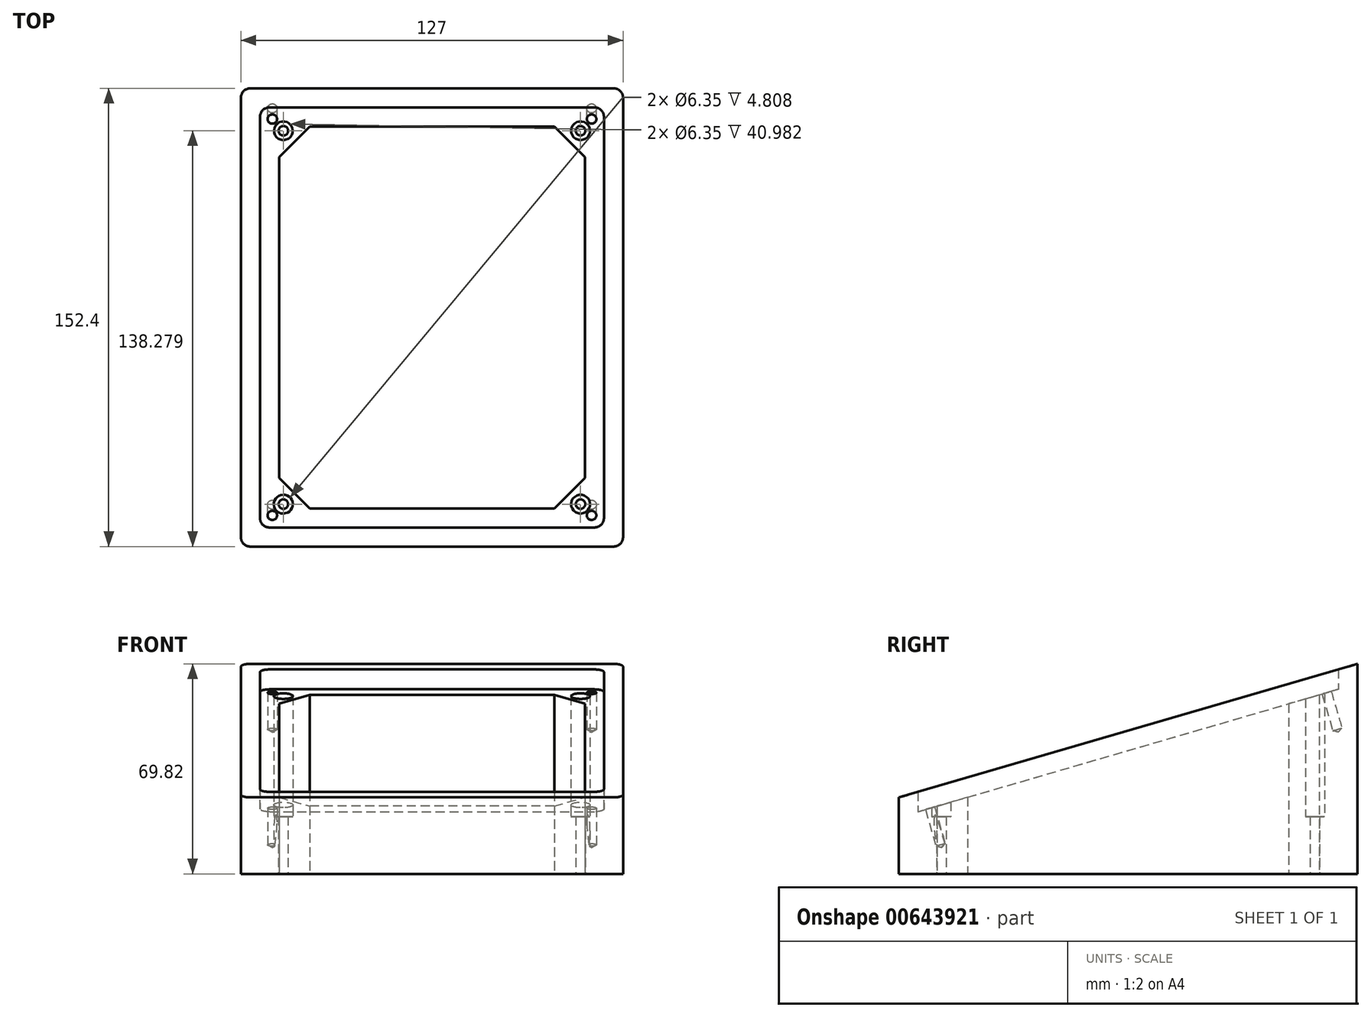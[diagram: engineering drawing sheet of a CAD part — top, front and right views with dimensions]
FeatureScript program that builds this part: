
annotation { "Feature Type Name" : "Feature", "Feature Type Description" : "" }
export const myFeature = defineFeature(function(context is Context, id is Id, definition is map)
    precondition{}
    {
        {
            var Q0;
            Q0=qCreatedBy(makeId("Top.planeOp"),FACE);
            var sketch = newSketch(context, id + "F0", { "sketchPlane" : qUnion([Q0])});
            skLineSegment(sketch, "E0.bottom", {"start": v(-63.5, 77.08) * mm, "end": v(63.5, 77.08) * mm});
            skLineSegment(sketch, "E0.top", {"start": v(-63.5, -75.32) * mm, "end": v(63.5, -75.32) * mm});
            skLineSegment(sketch, "E0.left", {"start": v(-63.5, 77.08) * mm, "end": v(-63.5, -75.32) * mm});
            skLineSegment(sketch, "E0.right", {"start": v(63.5, 77.08) * mm, "end": v(63.5, -75.32) * mm});
            skPoint(sketch, "E0.middle", {"position": v(0, 0.88) * mm});
            skLineSegment(sketch, "E1.bottom", {"start": v(-53.98, 70.73) * mm, "end": v(53.97, 70.73) * mm});
            skLineSegment(sketch, "E1.top", {"start": v(-53.98, -68.97) * mm, "end": v(53.97, -68.97) * mm});
            skLineSegment(sketch, "E1.left", {"start": v(-57.15, 67.56) * mm, "end": v(-57.15, -65.8) * mm});
            skLineSegment(sketch, "E1.right", {"start": v(57.15, 67.56) * mm, "end": v(57.15, -65.8) * mm});
            skLineSegment(sketch, "E2.bottom", {"start": v(-47.63, 64.38) * mm, "end": v(47.62, 64.38) * mm});
            skLineSegment(sketch, "E2.top", {"start": v(-47.63, -62.62) * mm, "end": v(48.25, -62.62) * mm});
            skLineSegment(sketch, "E2.left", {"start": v(-50.8, 61.2) * mm, "end": v(-50.8, -59.44) * mm});
            skLineSegment(sketch, "E2.right", {"start": v(50.8, 61.2) * mm, "end": v(50.8, -60.07) * mm});
            skPoint(sketch, "E3.visualSharp", {"position": v(-57.15, 70.73) * mm});
            skArc(sketch, "E3.filletArc", {"start": v(-53.98, 70.73) * mm, "mid": v(-56.22, 69.8) * mm, "end": v(-57.15, 67.56) * mm});
            skPoint(sketch, "E4.visualSharp", {"position": v(57.15, 70.73) * mm});
            skArc(sketch, "E4.filletArc", {"start": v(57.15, 67.56) * mm, "mid": v(56.22, 69.8) * mm, "end": v(53.97, 70.73) * mm});
            skPoint(sketch, "E5.visualSharp", {"position": v(57.15, -68.97) * mm});
            skArc(sketch, "E5.filletArc", {"start": v(53.97, -68.97) * mm, "mid": v(56.22, -68.04) * mm, "end": v(57.15, -65.8) * mm});
            skPoint(sketch, "E6.visualSharp", {"position": v(-57.15, -68.97) * mm});
            skArc(sketch, "E6.filletArc", {"start": v(-57.15, -65.8) * mm, "mid": v(-56.22, -68.04) * mm, "end": v(-53.98, -68.97) * mm});
            skPoint(sketch, "E7.visualSharp", {"position": v(50.8, 64.38) * mm});
            skArc(sketch, "E7.filletArc", {"start": v(50.8, 61.2) * mm, "mid": v(49.87, 63.45) * mm, "end": v(47.62, 64.38) * mm});
            skPoint(sketch, "E8.visualSharp", {"position": v(50.8, -62.62) * mm});
            skArc(sketch, "E8.filletArc", {"start": v(48.25, -62.62) * mm, "mid": v(50.05, -61.87) * mm, "end": v(50.8, -60.07) * mm});
            skPoint(sketch, "E9.visualSharp", {"position": v(-50.8, -62.62) * mm});
            skArc(sketch, "E9.filletArc", {"start": v(-50.8, -59.44) * mm, "mid": v(-49.87, -61.69) * mm, "end": v(-47.63, -62.62) * mm});
            skArc(sketch, "E10.filletArc", {"start": v(-47.63, 64.38) * mm, "mid": v(-49.87, 63.45) * mm, "end": v(-50.8, 61.2) * mm});
            skPoint(sketch, "E11.visualSharp", {"position": v(-63.5, 77.08) * mm});
            skLineSegment(sketch, "E11.filletArc", {"start": v(-63.5, 77.08) * mm, "end": v(-63.5, 77.08) * mm});
            skPoint(sketch, "E12.visualSharp", {"position": v(63.5, 77.08) * mm});
            skLineSegment(sketch, "E12.filletArc", {"start": v(63.5, 77.08) * mm, "end": v(63.5, 77.08) * mm});
            skPoint(sketch, "E13.visualSharp", {"position": v(63.5, -75.32) * mm});
            skLineSegment(sketch, "E13.filletArc", {"start": v(63.5, -75.32) * mm, "end": v(63.5, -75.32) * mm});
            skPoint(sketch, "E14.visualSharp", {"position": v(-63.5, -75.32) * mm});
            skLineSegment(sketch, "E14.filletArc", {"start": v(-63.5, -75.32) * mm, "end": v(-63.5, -75.32) * mm});
            skPoint(sketch, "E15", {"position": v(15.87, 64.38) * mm});
            skPoint(sketch, "E16", {"position": v(15.87, 77.08) * mm});
            skPoint(sketch, "E17", {"position": v(15.87, -62.62) * mm});
            skPoint(sketch, "E18", {"position": v(15.87, -75.32) * mm});
            skPoint(sketch, "E19", {"position": v(-15.88, 77.08) * mm});
            skPoint(sketch, "E20", {"position": v(-15.88, 64.38) * mm});
            skPoint(sketch, "E21", {"position": v(-15.88, -62.62) * mm});
            skPoint(sketch, "E22", {"position": v(-15.88, -75.32) * mm});
            skPoint(sketch, "E23", {"position": v(0, 77.08) * mm});
            skPoint(sketch, "E24", {"position": v(0, -75.32) * mm});
            skPoint(sketch, "E25", {"position": v(-63.5, 0.88) * mm});
            skPoint(sketch, "E26", {"position": v(63.5, 0.88) * mm});
            skPoint(sketch, "E27", {"position": v(63.5, 16.76) * mm});
            skPoint(sketch, "E28", {"position": v(50.8, 16.76) * mm});
            skPoint(sketch, "E29", {"position": v(-50.8, 16.76) * mm});
            skPoint(sketch, "E30", {"position": v(-63.5, 16.76) * mm});
            skPoint(sketch, "E31", {"position": v(63.5, -15) * mm});
            skPoint(sketch, "E32", {"position": v(50.8, -15) * mm});
            skPoint(sketch, "E33", {"position": v(-50.8, -15) * mm});
            skPoint(sketch, "E34", {"position": v(-63.5, -15) * mm});
            skPoint(sketch, "E35", {"position": v(40.64, 64.38) * mm});
            skPoint(sketch, "E36", {"position": v(40.64, -62.62) * mm});
            skPoint(sketch, "E37", {"position": v(-40.64, 64.38) * mm});
            skPoint(sketch, "E38", {"position": v(-40.64, -62.62) * mm});
            skPoint(sketch, "E39", {"position": v(-50.8, -52.46) * mm});
            skPoint(sketch, "E40", {"position": v(50.8, -52.46) * mm});
            skPoint(sketch, "E41", {"position": v(50.8, 54.22) * mm});
            skPoint(sketch, "E42", {"position": v(-50.8, 54.22) * mm});
            skLineSegment(sketch, "E43", {"start": v(-50.8, 54.22) * mm, "end": v(-40.64, 64.38) * mm});
            skLineSegment(sketch, "E44", {"start": v(40.64, 64.38) * mm, "end": v(50.8, 54.22) * mm});
            skLineSegment(sketch, "E45", {"start": v(50.8, -52.46) * mm, "end": v(40.64, -62.62) * mm});
            skLineSegment(sketch, "E46", {"start": v(-40.64, -62.62) * mm, "end": v(-50.8, -52.46) * mm});
            skPoint(sketch, "E47", {"position": v(-45.72, 59.3) * mm});
            skPoint(sketch, "E48", {"position": v(45.72, 59.3) * mm});
            skPoint(sketch, "E49", {"position": v(45.72, -57.54) * mm});
            skPoint(sketch, "E50", {"position": v(-45.72, -57.54) * mm});
            skPoint(sketch, "E51", {"position": v(30.16, 77.08) * mm});
            skPoint(sketch, "E52", {"position": v(30.16, 64.38) * mm});
            skPoint(sketch, "E53", {"position": v(30.16, -62.62) * mm});
            skPoint(sketch, "E54", {"position": v(30.16, -75.32) * mm});
            skPoint(sketch, "E55", {"position": v(-30.16, 77.08) * mm});
            skPoint(sketch, "E56", {"position": v(-30.16, 64.38) * mm});
            skPoint(sketch, "E57", {"position": v(-30.16, -62.62) * mm});
            skPoint(sketch, "E58", {"position": v(-30.16, -75.32) * mm});
            skPoint(sketch, "E59", {"position": v(63.5, 37.4) * mm});
            skPoint(sketch, "E60", {"position": v(50.8, 37.4) * mm});
            skPoint(sketch, "E61", {"position": v(-50.8, 37.4) * mm});
            skPoint(sketch, "E62", {"position": v(-63.5, 37.4) * mm});
            skPoint(sketch, "E63", {"position": v(63.5, -35.63) * mm});
            skPoint(sketch, "E64", {"position": v(50.8, -35.63) * mm});
            skPoint(sketch, "E65", {"position": v(-50.8, -35.63) * mm});
            skPoint(sketch, "E66", {"position": v(-63.5, -35.63) * mm});
            skPoint(sketch, "E67", {"position": v(-36.51, 77.08) * mm});
            skPoint(sketch, "E68", {"position": v(-36.51, 64.38) * mm});
            skPoint(sketch, "E69", {"position": v(-36.51, -62.62) * mm});
            skPoint(sketch, "E70", {"position": v(-36.51, -75.32) * mm});
            skPoint(sketch, "E71", {"position": v(36.51, 77.08) * mm});
            skPoint(sketch, "E72", {"position": v(36.51, 64.38) * mm});
            skPoint(sketch, "E73", {"position": v(36.51, -62.62) * mm});
            skPoint(sketch, "E74", {"position": v(36.51, -75.32) * mm});
            skPoint(sketch, "E75", {"position": v(-23.81, 77.08) * mm});
            skPoint(sketch, "E76", {"position": v(-23.81, 64.38) * mm});
            skPoint(sketch, "E77", {"position": v(23.81, 77.08) * mm});
            skPoint(sketch, "E78", {"position": v(23.81, 64.38) * mm});
            skPoint(sketch, "E79", {"position": v(23.81, -62.62) * mm});
            skPoint(sketch, "E80", {"position": v(23.81, -75.32) * mm});
            skPoint(sketch, "E81", {"position": v(-23.81, -62.62) * mm});
            skPoint(sketch, "E82", {"position": v(-23.81, -75.32) * mm});
            skPoint(sketch, "E83", {"position": v(-63.5, 43.74) * mm});
            skPoint(sketch, "E84", {"position": v(-50.8, 43.74) * mm});
            skPoint(sketch, "E85", {"position": v(50.8, 43.74) * mm});
            skPoint(sketch, "E86", {"position": v(63.5, 43.74) * mm});
            skPoint(sketch, "E87", {"position": v(-63.5, 31.04) * mm});
            skPoint(sketch, "E88", {"position": v(-50.8, 31.04) * mm});
            skPoint(sketch, "E89", {"position": v(50.8, 31.04) * mm});
            skPoint(sketch, "E90", {"position": v(63.5, 31.04) * mm});
            skPoint(sketch, "E91", {"position": v(-63.5, -29.28) * mm});
            skPoint(sketch, "E92", {"position": v(-50.8, -29.28) * mm});
            skPoint(sketch, "E93", {"position": v(50.8, -29.28) * mm});
            skPoint(sketch, "E94", {"position": v(63.5, -29.28) * mm});
            skPoint(sketch, "E95", {"position": v(-63.5, -41.98) * mm});
            skPoint(sketch, "E96", {"position": v(-50.8, -41.98) * mm});
            skPoint(sketch, "E97", {"position": v(50.8, -41.98) * mm});
            skPoint(sketch, "E98", {"position": v(63.5, -41.98) * mm});
            skLineSegment(sketch, "E99", {"start": v(57.15, 70.73) * mm, "end": v(45.72, 59.3) * mm, "construction": true});
            skLineSegment(sketch, "E100", {"start": v(57.15, -68.97) * mm, "end": v(45.72, -57.54) * mm, "construction": true});
            skLineSegment(sketch, "E101", {"start": v(-57.15, -68.97) * mm, "end": v(-45.72, -57.54) * mm, "construction": true});
            skPoint(sketch, "E102", {"position": v(53.04, 66.62) * mm});
            skLineSegment(sketch, "E103", {"start": v(-57.15, 70.73) * mm, "end": v(-45.72, 59.3) * mm, "construction": true});
            skPoint(sketch, "E104", {"position": v(-53.04, 66.62) * mm});
            skPoint(sketch, "E105", {"position": v(53.04, -64.86) * mm});
            skPoint(sketch, "E106", {"position": v(-53.04, -64.86) * mm});
            skCircle(sketch, "E107", {"center": v(-53.04, 66.62) * mm, "radius": 1.59 * mm});
            skCircle(sketch, "E108", {"center": v(53.04, 66.62) * mm, "radius": 1.59 * mm});
            skCircle(sketch, "E109", {"center": v(53.04, -64.86) * mm, "radius": 1.59 * mm});
            skCircle(sketch, "E110", {"center": v(-53.04, -64.86) * mm, "radius": 1.59 * mm});
            skPoint(sketch, "E111", {"position": v(-49.38, -61.2) * mm});
            skPoint(sketch, "E112", {"position": v(49.38, -61.2) * mm});
            skCircle(sketch, "E113", {"center": v(-49.38, -61.2) * mm, "radius": 1.59 * mm});
            skCircle(sketch, "E114", {"center": v(49.38, -61.2) * mm, "radius": 1.59 * mm});
            skPoint(sketch, "E115", {"position": v(-49.38, 62.96) * mm});
            skPoint(sketch, "E116", {"position": v(49.38, 62.96) * mm});
            skCircle(sketch, "E117", {"center": v(-49.38, 62.96) * mm, "radius": 1.59 * mm});
            skCircle(sketch, "E118", {"center": v(49.38, 62.96) * mm, "radius": 1.59 * mm});
            skCircle(sketch, "E119", {"center": v(-49.38, 62.96) * mm, "radius": 3.18 * mm});
            skCircle(sketch, "E120", {"center": v(49.38, 62.96) * mm, "radius": 3.18 * mm});
            skCircle(sketch, "E121", {"center": v(-49.38, -61.2) * mm, "radius": 3.18 * mm});
            skCircle(sketch, "E122", {"center": v(49.38, -61.2) * mm, "radius": 3.18 * mm});
            skSolve(sketch);
        }
        {
            var Q0;
            Q0=makeQuery(id+"F0.imprint","IMPRINT",FACE,{"disambiguationData":[TD([[makeQuery(id+"F0.imprint","IMPRINT",EDGE,{"derivedFrom":sQuery(id+"F0.wireOp",EDGE,"E0.bottom")}),-1.0]])]});
            var Q1;
            Q1=makeQuery(id+"F0.imprint","IMPRINT",FACE,{"disambiguationData":[TD([[makeQuery(id+"F0.imprint","IMPRINT",EDGE,{"derivedFrom":sQuery(id+"F0.wireOp",EDGE,"E1.bottom")}),-1.0]])]});
            var Q2;
            {var subQ5=sQuery(id+"F0.wireOp",EDGE,"E43");Q2=makeQuery(id+"F0.imprint","IMPRINT",FACE,{"disambiguationData":[TD([[makeQuery(id+"F0.imprint","IMPRINT",EDGE,{"derivedFrom":subQ5}),1.0]])]});}
            var Q3;
            {var subQ8=sQuery(id+"F0.wireOp",EDGE,"E44");Q3=makeQuery(id+"F0.imprint","IMPRINT",FACE,{"disambiguationData":[TD([[makeQuery(id+"F0.imprint","IMPRINT",EDGE,{"derivedFrom":subQ8}),1.0]])]});}
            var Q4;
            {var subQ8=sQuery(id+"F0.wireOp",EDGE,"E45");Q4=makeQuery(id+"F0.imprint","IMPRINT",FACE,{"disambiguationData":[TD([[makeQuery(id+"F0.imprint","IMPRINT",EDGE,{"derivedFrom":subQ8}),1.0]])]});}
            var Q5;
            {var subQ5=sQuery(id+"F0.wireOp",EDGE,"E46");Q5=makeQuery(id+"F0.imprint","IMPRINT",FACE,{"disambiguationData":[TD([[makeQuery(id+"F0.imprint","IMPRINT",EDGE,{"derivedFrom":subQ5}),1.0]])]});}
            var Q6;
            Q6=makeQuery(id+"F0.imprint","IMPRINT",FACE,{"disambiguationData":[TD([[makeQuery(id+"F0.imprint","IMPRINT",EDGE,{"derivedFrom":sQuery(id+"F0.wireOp",EDGE,"E108")}),1.0]])]});
            var Q7;
            Q7=makeQuery(id+"F0.imprint","IMPRINT",FACE,{"disambiguationData":[TD([[makeQuery(id+"F0.imprint","IMPRINT",EDGE,{"derivedFrom":sQuery(id+"F0.wireOp",EDGE,"E107")}),1.0]])]});
            var Q8;
            Q8=makeQuery(id+"F0.imprint","IMPRINT",FACE,{"disambiguationData":[TD([[makeQuery(id+"F0.imprint","IMPRINT",EDGE,{"derivedFrom":sQuery(id+"F0.wireOp",EDGE,"E109")}),1.0]])]});
            var Q9;
            Q9=makeQuery(id+"F0.imprint","IMPRINT",FACE,{"disambiguationData":[TD([[makeQuery(id+"F0.imprint","IMPRINT",EDGE,{"derivedFrom":sQuery(id+"F0.wireOp",EDGE,"E110")}),1.0]])]});
            extrude(context, id + "F1", {"entities" : qUnion([Q0, Q1, Q2, Q3, Q4, Q5, Q6, Q7, Q8, Q9]), "depth" : 76.2 * mm, "offsetDistance" : 25.4 * mm});
        }
        {
            var Q0;
            Q0=makeQuery(id+"F1.opExtrude","SWEPT_FACE",FACE,{"disambiguationData":[OSD([sQuery(id+"F0.wireOp",EDGE,"E0.right")])]});
            var sketch = newSketch(context, id + "F2", { "sketchPlane" : qUnion([Q0])});
            skPoint(sketch, "E123", {"position": v(77.08, 25.4) * mm});
            skPoint(sketch, "E124", {"position": v(77.08, 69.85) * mm});
            skPoint(sketch, "E125", {"position": v(-75.38, 25.4) * mm});
            skPoint(sketch, "E126", {"position": v(77.18, 69.85) * mm});
            skLineSegment(sketch, "E127", {"start": v(-75.38, 25.4) * mm, "end": v(77.18, 69.85) * mm});
            skLineSegment(sketch, "E128", {"start": v(77.18, 69.85) * mm, "end": v(77.18, 82.96) * mm});
            skLineSegment(sketch, "E129", {"start": v(77.18, 82.96) * mm, "end": v(-75.38, 82.96) * mm});
            skLineSegment(sketch, "E130", {"start": v(-75.38, 82.96) * mm, "end": v(-75.38, 25.4) * mm});
            skSolve(sketch);
        }
        {
            var Q0;
            Q0 = qSketchRegion(id + "F2", true);
            extrude(context, id + "F3", {"entities" : qUnion([Q0]), "operationType" : NewBodyOperationType.REMOVE, "oppositeDirection" : true, "depth" : 133.86 * mm, "offsetDistance" : 25.4 * mm});
        }
        {
            var Q0;
            Q0=makeQuery(id+"F1.opExtrude","SWEPT_FACE",FACE,{"disambiguationData":[OSD([sQuery(id+"F0.wireOp",EDGE,"E0.right")])]});
            var sketch = newSketch(context, id + "F4", { "sketchPlane" : qUnion([Q0])});
            skPoint(sketch, "E131", {"position": v(-75.32, 19.07) * mm});
            skPoint(sketch, "E132", {"position": v(-68.97, 19.07) * mm});
            skPoint(sketch, "E133", {"position": v(77.08, 63.47) * mm});
            skPoint(sketch, "E134", {"position": v(-68.97, 27.27) * mm});
            skPoint(sketch, "E135", {"position": v(70.73, 67.97) * mm});
            skPoint(sketch, "E136", {"position": v(-68.97, 20.66) * mm});
            skPoint(sketch, "E137", {"position": v(70.73, 61.36) * mm});
            skPoint(sketch, "E138", {"position": v(70.73, 71.15) * mm});
            skPoint(sketch, "E139", {"position": v(-68.97, 30.44) * mm});
            skLineSegment(sketch, "E140", {"start": v(-68.97, 20.66) * mm, "end": v(70.73, 61.36) * mm});
            skLineSegment(sketch, "E141", {"start": v(70.73, 71.15) * mm, "end": v(70.73, 61.36) * mm});
            skLineSegment(sketch, "E142", {"start": v(-68.97, 30.44) * mm, "end": v(-68.97, 20.66) * mm});
            skLineSegment(sketch, "E143", {"start": v(-68.97, 30.44) * mm, "end": v(70.73, 71.15) * mm});
            skPoint(sketch, "E144", {"position": v(-75.32, 25.42) * mm});
            skPoint(sketch, "E145", {"position": v(-75.32, 0) * mm});
            skPoint(sketch, "E146", {"position": v(77.08, 69.82) * mm});
            skPoint(sketch, "E147", {"position": v(77.08, 0) * mm});
            skSolve(sketch);
        }
        {
            var Q0;
            {var subQ0=sQuery(id+"F4.wireOp",EDGE,"E140");Q0=makeQuery(id+"F4.imprint","IMPRINT",FACE,{"disambiguationData":[TD([[makeQuery(id+"F4.imprint","IMPRINT",EDGE,{"derivedFrom":subQ0}),1.0]])]});}
            var Q1;
            {var subQ0=sQuery(id+"F4.wireOp",EDGE,"E143");Q1=makeQuery(id+"F4.imprint","IMPRINT",FACE,{"disambiguationData":[TD([[makeQuery(id+"F4.imprint","IMPRINT",EDGE,{"derivedFrom":subQ0}),-1.0]])]});}
            extrude(context, id + "F5", {"entities" : qUnion([Q0, Q1]), "operationType" : NewBodyOperationType.REMOVE, "oppositeDirection" : true, "depth" : 120.65 * mm, "offsetDistance" : 25.4 * mm, "hasSecondDirection" : true, "secondDirectionOppositeDirection" : true, "secondDirectionDepth" : 6.35 * mm});
        }
        {
            var Q0;
            Q0=makeQuery(id+"F5.boolean.opBoolean","COPY",FACE,{"derivedFrom":makeQuery(id+"F5.opExtrude","SWEPT_FACE",FACE,{"disambiguationData":[OSD([sQuery(id+"F4.wireOp",EDGE,"E140")])]})});
            var sketch = newSketch(context, id + "F6", { "sketchPlane" : qUnion([Q0])});
            skPoint(sketch, "E148", {"position": v(-57.15, 85.07) * mm});
            skPoint(sketch, "E149", {"position": v(57.15, 85.07) * mm});
            skPoint(sketch, "E150", {"position": v(57.15, -60.44) * mm});
            skPoint(sketch, "E151", {"position": v(-57.15, -60.44) * mm});
            skPoint(sketch, "E152", {"position": v(-53.04, 81.03) * mm});
            skPoint(sketch, "E153", {"position": v(53.04, 81.03) * mm});
            skPoint(sketch, "E154", {"position": v(53.04, -56.25) * mm});
            skPoint(sketch, "E155", {"position": v(-53.04, -56.25) * mm});
            skSolve(sketch);
        }
        {
            var Q0;
            Q0=sQuery(id+"F6.wireOp",VERTEX,"E152");
            var Q1;
            Q1=sQuery(id+"F6.wireOp",VERTEX,"E153");
            var Q2;
            Q2=sQuery(id+"F6.wireOp",VERTEX,"E154");
            var Q3;
            Q3=sQuery(id+"F6.wireOp",VERTEX,"E155");
            var Q4;
            Q4=makeQuery(id+"F1.opExtrude","SWEPT_BODY",BODY,{"disambiguationData":[OSD([sQuery(id+"F0.wireOp",EDGE,"E0.bottom"),sQuery(id+"F0.wireOp",EDGE,"E0.top"),sQuery(id+"F0.wireOp",EDGE,"E0.left"),sQuery(id+"F0.wireOp",EDGE,"E0.right"),sQuery(id+"F0.wireOp",EDGE,"E2.bottom"),sQuery(id+"F0.wireOp",EDGE,"E2.top"),sQuery(id+"F0.wireOp",EDGE,"E2.left"),sQuery(id+"F0.wireOp",EDGE,"E2.right"),sQuery(id+"F0.wireOp",EDGE,"E43"),sQuery(id+"F0.wireOp",EDGE,"E44"),sQuery(id+"F0.wireOp",EDGE,"E45"),sQuery(id+"F0.wireOp",EDGE,"E46"),sQuery(id+"F0.wireOp",EDGE,"E113"),sQuery(id+"F0.wireOp",EDGE,"E114"),sQuery(id+"F0.wireOp",EDGE,"E117"),sQuery(id+"F0.wireOp",EDGE,"E118")])]});
            hole(context, id + "F7", {"style" : HoleStyle.SIMPLE, "endStyle" : HoleEndStyle.BLIND, "holeDiameter" : 3.17 * mm, "majorDiameter" : 6.35 * mm, "holeDepth" : 12.7 * mm, "isTappedThrough" : true, "tappedDepth" : 12.7 * mm, "tapClearance" : 3, "locations" : qUnion([Q0, Q1, Q2, Q3]), "scope" : qUnion([Q4])});
        }
        {
            var Q0;
            Q0=makeQuery(id+"F5.boolean.opBoolean","COPY",EDGE,{"derivedFrom":makeQuery(id+"F5.opExtrude","CAP_EDGE",EDGE,{"disambiguationData":[OSD([sQuery(id+"F4.wireOp",EDGE,"E142")])],"isStart":false})});
            var Q1;
            Q1=makeQuery(id+"F5.boolean.opBoolean","COPY",EDGE,{"derivedFrom":makeQuery(id+"F5.opExtrude","CAP_EDGE",EDGE,{"disambiguationData":[OSD([sQuery(id+"F4.wireOp",EDGE,"E142")])],"isStart":true})});
            var Q2;
            Q2=makeQuery(id+"F5.boolean.opBoolean","COPY",EDGE,{"derivedFrom":makeQuery(id+"F5.opExtrude","CAP_EDGE",EDGE,{"disambiguationData":[OSD([sQuery(id+"F4.wireOp",EDGE,"E141")])],"isStart":false})});
            var Q3;
            Q3=makeQuery(id+"F5.boolean.opBoolean","COPY",EDGE,{"derivedFrom":makeQuery(id+"F5.opExtrude","CAP_EDGE",EDGE,{"disambiguationData":[OSD([sQuery(id+"F4.wireOp",EDGE,"E141")])],"isStart":true})});
            fillet(context, id + "F8", {"entities" : qUnion([Q0, Q1, Q2, Q3]), "radius" : 3.17 * mm, "tangentPropagation" : true, "allowEdgeOverflow" : false});
        }
        {
            var Q0;
            {var subQ0=sQuery(id+"F0.wireOp",EDGE,"E10.filletArc");var subQ1=sQuery(id+"F0.wireOp",EDGE,"E2.bottom");var subQ2=makeQuery(id+"F0.imprint","INTERSECT",VERTEX,{"derivedFrom":[subQ1,subQ0]});Q0=makeQuery(id+"F0.imprint","IMPRINT",FACE,{"disambiguationData":[TD([[makeQuery(id+"F0.imprint","IMPRINT",EDGE,{"disambiguationData":[TD([[subQ2,-1.0]])],"derivedFrom":subQ1}),-1.0]])]});}
            var Q1;
            {var subQ0=sQuery(id+"F0.wireOp",EDGE,"E10.filletArc");var subQ1=sQuery(id+"F0.wireOp",EDGE,"E2.bottom");var subQ2=makeQuery(id+"F0.imprint","INTERSECT",VERTEX,{"derivedFrom":[subQ1,subQ0]});Q1=makeQuery(id+"F0.imprint","IMPRINT",FACE,{"disambiguationData":[TD([[makeQuery(id+"F0.imprint","IMPRINT",EDGE,{"disambiguationData":[TD([[subQ2,-1.0]])],"derivedFrom":subQ1}),1.0]])]});}
            var Q2;
            {var subQ0=sQuery(id+"F0.wireOp",EDGE,"E7.filletArc");var subQ1=sQuery(id+"F0.wireOp",EDGE,"E2.bottom");var subQ2=makeQuery(id+"F0.imprint","INTERSECT",VERTEX,{"derivedFrom":[subQ1,subQ0]});Q2=makeQuery(id+"F0.imprint","IMPRINT",FACE,{"disambiguationData":[TD([[makeQuery(id+"F0.imprint","IMPRINT",EDGE,{"disambiguationData":[TD([[subQ2,1.0]])],"derivedFrom":subQ1}),-1.0]])]});}
            var Q3;
            {var subQ0=sQuery(id+"F0.wireOp",EDGE,"E7.filletArc");var subQ1=sQuery(id+"F0.wireOp",EDGE,"E2.bottom");var subQ2=makeQuery(id+"F0.imprint","INTERSECT",VERTEX,{"derivedFrom":[subQ1,subQ0]});Q3=makeQuery(id+"F0.imprint","IMPRINT",FACE,{"disambiguationData":[TD([[makeQuery(id+"F0.imprint","IMPRINT",EDGE,{"disambiguationData":[TD([[subQ2,1.0]])],"derivedFrom":subQ1}),1.0]])]});}
            var Q4;
            {var subQ0=sQuery(id+"F0.wireOp",EDGE,"E8.filletArc");var subQ1=sQuery(id+"F0.wireOp",EDGE,"E2.top");var subQ2=makeQuery(id+"F0.imprint","INTERSECT",VERTEX,{"derivedFrom":[subQ1,subQ0]});Q4=makeQuery(id+"F0.imprint","IMPRINT",FACE,{"disambiguationData":[TD([[makeQuery(id+"F0.imprint","IMPRINT",EDGE,{"disambiguationData":[TD([[subQ2,1.0]])],"derivedFrom":subQ1}),-1.0]])]});}
            var Q5;
            {var subQ0=sQuery(id+"F0.wireOp",EDGE,"E8.filletArc");var subQ1=sQuery(id+"F0.wireOp",EDGE,"E2.top");var subQ2=makeQuery(id+"F0.imprint","INTERSECT",VERTEX,{"derivedFrom":[subQ1,subQ0]});Q5=makeQuery(id+"F0.imprint","IMPRINT",FACE,{"disambiguationData":[TD([[makeQuery(id+"F0.imprint","IMPRINT",EDGE,{"disambiguationData":[TD([[subQ2,1.0]])],"derivedFrom":subQ1}),1.0]])]});}
            var Q6;
            {var subQ0=sQuery(id+"F0.wireOp",EDGE,"E9.filletArc");var subQ1=sQuery(id+"F0.wireOp",EDGE,"E2.top");var subQ2=makeQuery(id+"F0.imprint","INTERSECT",VERTEX,{"derivedFrom":[subQ1,subQ0]});Q6=makeQuery(id+"F0.imprint","IMPRINT",FACE,{"disambiguationData":[TD([[makeQuery(id+"F0.imprint","IMPRINT",EDGE,{"disambiguationData":[TD([[subQ2,-1.0]])],"derivedFrom":subQ1}),-1.0]])]});}
            var Q7;
            {var subQ0=sQuery(id+"F0.wireOp",EDGE,"E9.filletArc");var subQ1=sQuery(id+"F0.wireOp",EDGE,"E2.top");var subQ2=makeQuery(id+"F0.imprint","INTERSECT",VERTEX,{"derivedFrom":[subQ1,subQ0]});Q7=makeQuery(id+"F0.imprint","IMPRINT",FACE,{"disambiguationData":[TD([[makeQuery(id+"F0.imprint","IMPRINT",EDGE,{"disambiguationData":[TD([[subQ2,-1.0]])],"derivedFrom":subQ1}),1.0]])]});}
            extrude(context, id + "F9", {"entities" : qUnion([Q0, Q1, Q2, Q3, Q4, Q5, Q6, Q7]), "operationType" : NewBodyOperationType.ADD, "depth" : 19.05 * mm, "offsetDistance" : 25.4 * mm});
        }
        {
            var Q0;
            Q0=makeQuery(id+"F1.opExtrude","SWEPT_EDGE",EDGE,{"disambiguationData":[OSD([sQuery(id+"F0.wireOp",EDGE,"E0.bottom"),sQuery(id+"F0.wireOp",EDGE,"E0.left")])]});
            var Q1;
            Q1=makeQuery(id+"F1.opExtrude","SWEPT_EDGE",EDGE,{"disambiguationData":[OSD([sQuery(id+"F0.wireOp",EDGE,"E0.top"),sQuery(id+"F0.wireOp",EDGE,"E0.left")])]});
            var Q2;
            Q2=makeQuery(id+"F1.opExtrude","SWEPT_EDGE",EDGE,{"disambiguationData":[OSD([sQuery(id+"F0.wireOp",EDGE,"E0.bottom"),sQuery(id+"F0.wireOp",EDGE,"E0.right")])]});
            var Q3;
            Q3=makeQuery(id+"F1.opExtrude","SWEPT_EDGE",EDGE,{"disambiguationData":[OSD([sQuery(id+"F0.wireOp",EDGE,"E0.top"),sQuery(id+"F0.wireOp",EDGE,"E0.right")])]});
            fillet(context, id + "F10", {"entities" : qUnion([Q0, Q1, Q2, Q3]), "radius" : 3.17 * mm, "tangentPropagation" : true, "allowEdgeOverflow" : false});
        }
    });
